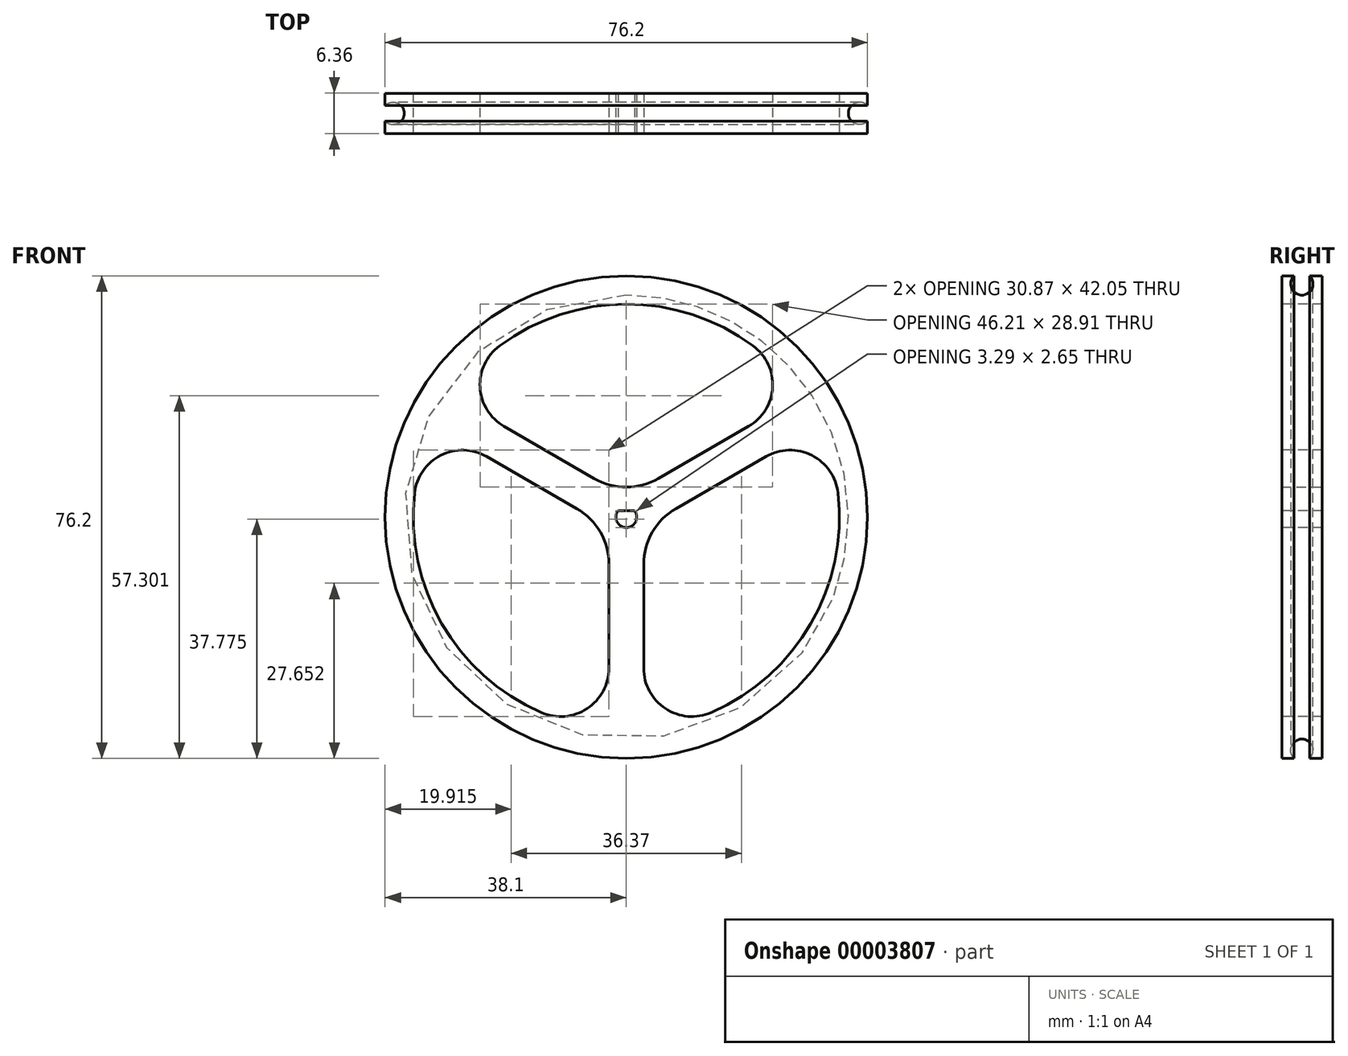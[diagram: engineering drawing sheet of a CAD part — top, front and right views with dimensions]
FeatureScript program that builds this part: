
annotation { "Feature Type Name" : "Feature", "Feature Type Description" : "" }
export const myFeature = defineFeature(function(context is Context, id is Id, definition is map)
    precondition{}
    {
        {
            var Q0;
            Q0=qCreatedBy(makeId("Front.planeOp"),FACE);
            var sketch = newSketch(context, id + "F0", { "sketchPlane" : qUnion([Q0])});
            skCircle(sketch, "E0", {"center": v(0, 0) * mm, "radius": 38.1 * mm});
            skSolve(sketch);
        }
        {
            var Q0;
            Q0 = qSketchRegion(id + "F0", true);
            extrude(context, id + "F1", {"entities" : qUnion([Q0]), "oppositeDirection" : true, "depth" : 3.17 * mm});
        }
        {
            var Q0;
            Q0 = qSketchRegion(id + "F0", true);
            extrude(context, id + "F2", {"entities" : qUnion([Q0]), "operationType" : NewBodyOperationType.ADD, "depth" : 3.17 * mm});
        }
        {
            var Q0;
            Q0=qCreatedBy(makeId("Right.planeOp"),FACE);
            var sketch = newSketch(context, id + "F3", { "sketchPlane" : qUnion([Q0])});
            skCircle(sketch, "E1", {"center": v(0, 36.83) * mm, "radius": 1.77 * mm});
            skLineSegment(sketch, "E2", {"start": v(0, 0) * mm, "end": v(24.73, 0) * mm, "construction": true});
            skSolve(sketch);
        }
        {
            var Q0;
            Q0 = qSketchRegion(id + "F3", true);
            var Q1;
            Q1=sQuery(id+"F3.wireOp",EDGE,"E2");
            revolve(context, id + "F4", {"operationType" : NewBodyOperationType.REMOVE, "entities" : qUnion([Q0]), "axis" : qUnion([Q1]), "revolveType" : RevolveType.FULL, "oppositeDirection" : true});
        }
        {
            var Q0;
            Q0=makeQuery(id+"F2.opExtrude","CAP_FACE",FACE,{"disambiguationData":[OSD([sQuery(id+"F0.wireOp",EDGE,"E0")])],"isStart":false});
            var sketch = newSketch(context, id + "F5", { "sketchPlane" : qUnion([Q0])});
            skArc(sketch, "E3", {"start": v(-1.31, 1) * mm, "mid": v(0, -1.65) * mm, "end": v(1.31, 1) * mm});
            skLineSegment(sketch, "E4", {"start": v(-1.31, 1) * mm, "end": v(1.31, 1) * mm});
            skSolve(sketch);
        }
        {
            var Q0;
            Q0 = qSketchRegion(id + "F5", true);
            extrude(context, id + "F6", {"entities" : qUnion([Q0]), "operationType" : NewBodyOperationType.REMOVE, "endBound" : BoundingType.THROUGH_ALL, "oppositeDirection" : true, "depth" : 25.4 * mm});
        }
        {
            var Q0;
            Q0=makeQuery(id+"F2.opExtrude","CAP_FACE",FACE,{"disambiguationData":[OSD([sQuery(id+"F0.wireOp",EDGE,"E0")])],"isStart":false});
            var sketch = newSketch(context, id + "F7", { "sketchPlane" : qUnion([Q0])});
            skCircle(sketch, "E5", {"center": v(0, 0) * mm, "radius": 33.66 * mm, "construction": true});
            skLineSegment(sketch, "E6", {"start": v(0, 0) * mm, "end": v(29.15, 16.83) * mm, "construction": true});
            skLineSegment(sketch, "E7", {"start": v(0, 0) * mm, "end": v(-29.15, 16.83) * mm, "construction": true});
            skLineSegment(sketch, "E8", {"start": v(0, 0) * mm, "end": v(0, 33.66) * mm, "construction": true});
            skLineSegment(sketch, "E9", {"start": v(0, 3.17) * mm, "end": v(-27.67, 19.15) * mm, "construction": true});
            skLineSegment(sketch, "E10", {"start": v(0, 3.17) * mm, "end": v(27.67, 19.15) * mm, "construction": true});
            skArc(sketch, "E11", {"start": v(27.67, 19.15) * mm, "mid": v(0, 33.66) * mm, "end": v(-27.67, 19.15) * mm, "construction": true});
            skLineSegment(sketch, "E12", {"start": v(-27.67, 19.15) * mm, "end": v(0, 3.18) * mm});
            skLineSegment(sketch, "E13", {"start": v(0, 3.17) * mm, "end": v(27.67, 19.15) * mm});
            skArc(sketch, "E14", {"start": v(27.67, 19.15) * mm, "mid": v(0, 33.66) * mm, "end": v(-27.67, 19.15) * mm});
            skArc(sketch, "E15.1.0", {"start": v(-30.42, 14.39) * mm, "mid": v(-29.15, -16.83) * mm, "end": v(-2.75, -33.54) * mm});
            skLineSegment(sketch, "E15.1.1", {"start": v(-2.75, -33.54) * mm, "end": v(-2.75, -1.59) * mm});
            skLineSegment(sketch, "E15.1.2", {"start": v(-2.75, -1.59) * mm, "end": v(-30.42, 14.39) * mm});
            skLineSegment(sketch, "E15.anchor1", {"start": v(0, 0) * mm, "end": v(-27.67, 19.15) * mm, "construction": true});
            skLineSegment(sketch, "E15.anchor2", {"start": v(0, 0) * mm, "end": v(30.42, 14.39) * mm, "construction": true});
            skArc(sketch, "E16.3.2.0", {"start": v(2.75, -33.54) * mm, "mid": v(29.15, -16.83) * mm, "end": v(30.42, 14.39) * mm});
            skLineSegment(sketch, "E16.4.2.0", {"start": v(30.42, 14.39) * mm, "end": v(2.75, -1.59) * mm});
            skLineSegment(sketch, "E16.7.2.0", {"start": v(2.75, -1.59) * mm, "end": v(2.75, -33.54) * mm});
            skSolve(sketch);
        }
        {
            var Q0;
            Q0=makeQuery(id+"F7.imprint","IMPRINT",FACE,{"disambiguationData":[TD([[makeQuery(id+"F7.imprint","IMPRINT",EDGE,{"derivedFrom":sQuery(id+"F7.wireOp",EDGE,"E12")}),1.0]])]});
            var Q1;
            Q1=makeQuery(id+"F7.imprint","IMPRINT",FACE,{"disambiguationData":[TD([[makeQuery(id+"F7.imprint","IMPRINT",EDGE,{"derivedFrom":sQuery(id+"F7.wireOp",EDGE,"E16.3.2.0")}),1.0]])]});
            var Q2;
            Q2=makeQuery(id+"F7.imprint","IMPRINT",FACE,{"disambiguationData":[TD([[makeQuery(id+"F7.imprint","IMPRINT",EDGE,{"derivedFrom":sQuery(id+"F7.wireOp",EDGE,"E15.1.0")}),1.0]])]});
            extrude(context, id + "F8", {"entities" : qUnion([Q0, Q1, Q2]), "operationType" : NewBodyOperationType.REMOVE, "endBound" : BoundingType.THROUGH_ALL, "oppositeDirection" : true, "depth" : 25.4 * mm});
        }
        {
            var Q0;
            Q0=makeQuery(id+"F8.boolean.opBoolean","COPY",EDGE,{"derivedFrom":makeQuery(id+"F8.opExtrude","SWEPT_EDGE",EDGE,{"disambiguationData":[OSD([sQuery(id+"F7.wireOp",EDGE,"E13"),sQuery(id+"F7.wireOp",EDGE,"E14")])]})});
            var Q1;
            Q1=makeQuery(id+"F8.boolean.opBoolean","COPY",EDGE,{"derivedFrom":makeQuery(id+"F8.opExtrude","SWEPT_EDGE",EDGE,{"disambiguationData":[OSD([sQuery(id+"F7.wireOp",EDGE,"E12"),sQuery(id+"F7.wireOp",EDGE,"E14")])]})});
            var Q2;
            Q2=makeQuery(id+"F8.boolean.opBoolean","COPY",EDGE,{"derivedFrom":makeQuery(id+"F8.opExtrude","SWEPT_EDGE",EDGE,{"disambiguationData":[OSD([sQuery(id+"F7.wireOp",EDGE,"E15.1.0"),sQuery(id+"F7.wireOp",EDGE,"E15.1.1")])]})});
            var Q3;
            Q3=makeQuery(id+"F8.boolean.opBoolean","COPY",EDGE,{"derivedFrom":makeQuery(id+"F8.opExtrude","SWEPT_EDGE",EDGE,{"disambiguationData":[OSD([sQuery(id+"F7.wireOp",EDGE,"E16.3.2.0"),sQuery(id+"F7.wireOp",EDGE,"E16.7.2.0")])]})});
            var Q4;
            Q4=makeQuery(id+"F8.boolean.opBoolean","COPY",EDGE,{"derivedFrom":makeQuery(id+"F8.opExtrude","SWEPT_EDGE",EDGE,{"disambiguationData":[OSD([sQuery(id+"F7.wireOp",EDGE,"E15.1.0"),sQuery(id+"F7.wireOp",EDGE,"E15.1.2")])]})});
            var Q5;
            Q5=makeQuery(id+"F8.boolean.opBoolean","COPY",EDGE,{"derivedFrom":makeQuery(id+"F8.opExtrude","SWEPT_EDGE",EDGE,{"disambiguationData":[OSD([sQuery(id+"F7.wireOp",EDGE,"E16.3.2.0"),sQuery(id+"F7.wireOp",EDGE,"E16.4.2.0")])]})});
            fillet(context, id + "F9", {"entities" : qUnion([Q0, Q1, Q2, Q3, Q4, Q5]), "radius" : 7.62 * mm, "tangentPropagation" : true, "allowEdgeOverflow" : false});
        }
        {
            var Q0;
            Q0=makeQuery(id+"F8.boolean.opBoolean","COPY",EDGE,{"derivedFrom":makeQuery(id+"F8.opExtrude","SWEPT_EDGE",EDGE,{"disambiguationData":[OSD([sQuery(id+"F7.wireOp",EDGE,"E12"),sQuery(id+"F7.wireOp",EDGE,"E13")])]})});
            var Q1;
            Q1=makeQuery(id+"F8.boolean.opBoolean","COPY",EDGE,{"derivedFrom":makeQuery(id+"F8.opExtrude","SWEPT_EDGE",EDGE,{"disambiguationData":[OSD([sQuery(id+"F7.wireOp",EDGE,"E15.1.1"),sQuery(id+"F7.wireOp",EDGE,"E15.1.2")])]})});
            var Q2;
            Q2=makeQuery(id+"F8.boolean.opBoolean","COPY",EDGE,{"derivedFrom":makeQuery(id+"F8.opExtrude","SWEPT_EDGE",EDGE,{"disambiguationData":[OSD([sQuery(id+"F7.wireOp",EDGE,"E16.4.2.0"),sQuery(id+"F7.wireOp",EDGE,"E16.7.2.0")])]})});
            fillet(context, id + "F10", {"entities" : qUnion([Q0, Q1, Q2]), "radius" : 10.16 * mm, "tangentPropagation" : true, "allowEdgeOverflow" : false});
        }
    });
